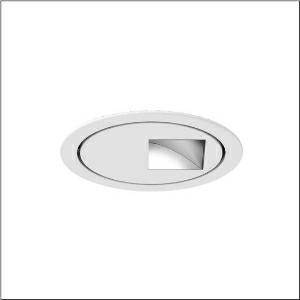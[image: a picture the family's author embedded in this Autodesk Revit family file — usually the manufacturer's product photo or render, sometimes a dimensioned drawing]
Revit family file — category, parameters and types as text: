
# Revit family: lunis_11_mini_round_51dk11cd2wn21
name_source: partatom
category: Lighting Fixtures
units: mm (PartAtom-declared; Revit-internal decimal feet)

## family parameters
Cut with Voids When Loaded = No
Host = Face
Light Source = No
Part Type = Normal
Room Calculation Point = No
Round Connector Dimension = Use Diameter
Shared = No

## types (1)
- Lunis 11 mini round (1 x LED 4000K / CRI = 90 (unbekannt), 2120 lm, 4000K)
    Apparent Load = 28 VA
    CIE Flux Codes = 44 77 97 100 100
    Color Rendering = 90
    Color Temperature = 4000K
    Default Elevation = 1800 mm
    Description = Lunis 11 mini round, downlight, light control with wallwasher, of highly reflective aluminium, highly specular, light emission: direct distribution, LED rated luminous flux: 2.120lm, light colour: 940, control gear: ECG, with terminal, 5-pole, mains connection: 220..230V, AC/DC, 0/50..60Hz, LED module, luminaire module, of aluminium, highly specular, white, diameter: 176mm, clamping range: 1..40mm, recessing ring, of plastic, traffic white (RAL 9016), protection rating (complete): IP20, insulation class (complete): insulation class II (safety insulation), certification: CE, permissible ambient temperature for indoor applications: 0..+35°C, packaging unit: 1 piece
    Height = 0 mm  [stored 0 ft]
    Lamp = 1 x LED 4000K / CRI >= 90 (unbekannt)
    Lamp Light Flux = 2120 lm
    Lamp count = 1
    Length = 176 mm
    Luminous efficacy = 76 lm/W
    Manufacturer = Siteco
    ModVariant = No
    Model = 51DK11CD2WN21
    Mounting Place = Ceiling
    Mounting Type = Recessed
    Number of Poles = 1
    OnlyDefault = Yes
    Power Factor = 1
    Product Name = Lunis 11 mini round
    Product group = downlight
    ProductGroupID = 400
    Protection Class = Protection class II
    Protection Degree = IP 20
    RLX_Detail_Level = 1
    RLX_Emergency_Light_Flux = 0 lm
    RLX_Emergency_Type = 0
    RLX_Emergency_Type_DB = No
    RlxData = <blob elided: 59329 chars, md5=33704cd1>
    Socket = socket
    Standby Power = 0 W
    System Light Flux = 2120 lm
    System Power = 28 W
    Type Comments = Product without accessories
    Type Image = l_1004772.jpg
    URL = http://relux.com
    VarID = ---
    Voltage = 0 V
    Weight = 0.00 kg
    Width = 176 mm

note: [stored X ft] marks values corroborated as IEEE doubles in the binary element streams (Revit-internal decimal feet)

## geometry (parser evidence)
native form markers: Blend x4, Sweep x9
no freeform markers — native parametric forms only
